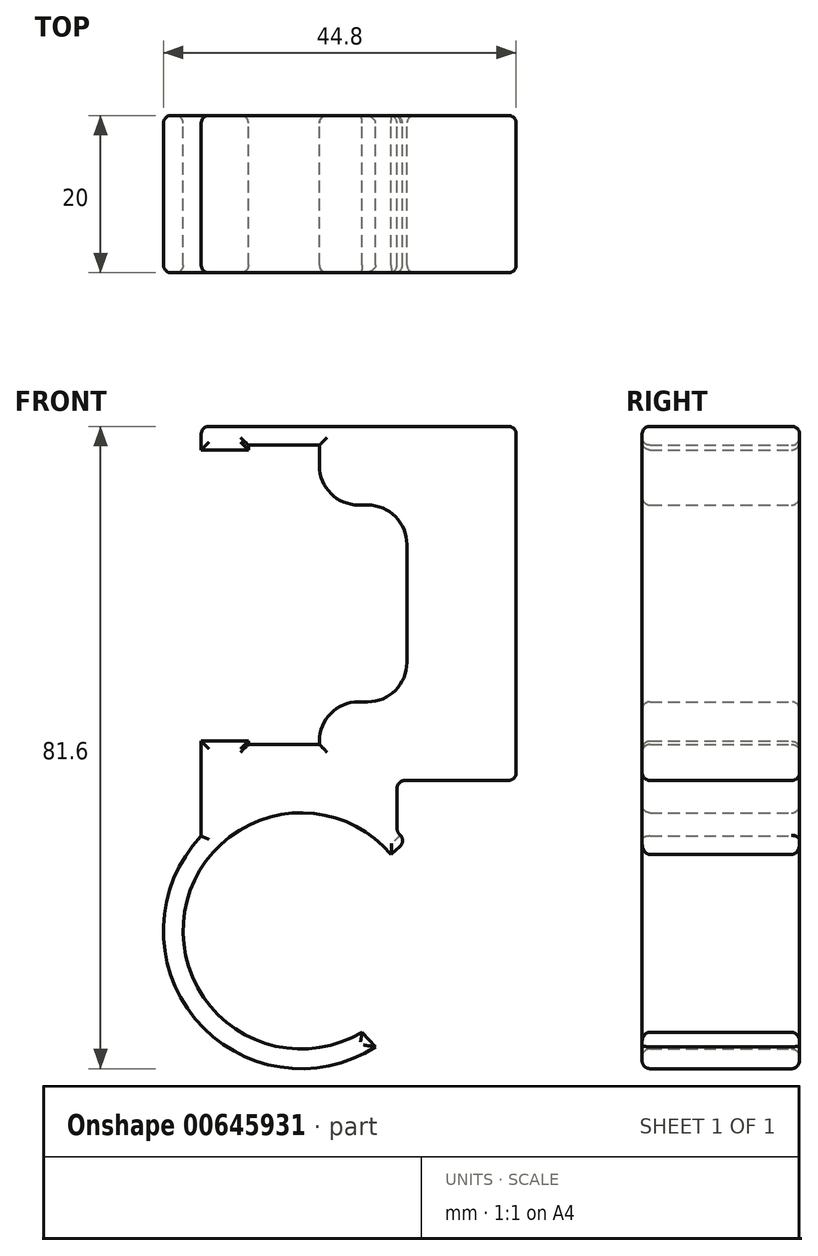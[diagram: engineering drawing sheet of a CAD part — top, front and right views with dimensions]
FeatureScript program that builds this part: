
annotation { "Feature Type Name" : "Feature", "Feature Type Description" : "" }
export const myFeature = defineFeature(function(context is Context, id is Id, definition is map)
    precondition{}
    {
        {
            var Q0;
            Q0=qCreatedBy(makeId("Front.planeOp"),FACE);
            var sketch = newSketch(context, id + "F0", { "sketchPlane" : qUnion([Q0])});
            skArc(sketch, "E0", {"start": v(11.43, 9.71) * mm, "mid": v(-14.8, 2.43) * mm, "end": v(7.72, -12.86) * mm});
            skArc(sketch, "E1", {"start": v(13.28, 11.4) * mm, "mid": v(12.74, 12) * mm, "end": v(12.17, 12.57) * mm});
            skLineSegment(sketch, "E2", {"start": v(11.43, 9.71) * mm, "end": v(13.28, 11.4) * mm});
            skLineSegment(sketch, "E3", {"start": v(7.72, -12.86) * mm, "end": v(9.47, -14.72) * mm});
            skLineSegment(sketch, "E4", {"start": v(-12.7, 17.5) * mm, "end": v(-12.7, 19.1) * mm});
            skLineSegment(sketch, "E5", {"start": v(-12.7, 19.1) * mm, "end": v(12.17, 19.1) * mm});
            skLineSegment(sketch, "E6", {"start": v(12.17, 19.1) * mm, "end": v(12.17, 17.5) * mm});
            skPoint(sketch, "E7.start.orphan", {"position": v(0, 17.5) * mm});
            skLineSegment(sketch, "E8", {"start": v(-12.7, 17.5) * mm, "end": v(-12.7, 12.04) * mm});
            skLineSegment(sketch, "E9", {"start": v(12.17, 17.5) * mm, "end": v(12.17, 12.57) * mm});
            skArc(sketch, "E10.trimOffspring", {"start": v(-12.7, 12.04) * mm, "mid": v(-13.48, -11.16) * mm, "end": v(9.47, -14.72) * mm});
            skSolve(sketch);
        }
        {
            var Q0;
            Q0=makeQuery(id+"F0.imprint","IMPRINT",FACE,{"disambiguationData":[TD([[makeQuery(id+"F0.imprint","IMPRINT",EDGE,{"derivedFrom":sQuery(id+"F0.wireOp",EDGE,"E0")}),-1.0]])]});
            var Q1;
            Q1=makeQuery(id+"F0.imprint","IMPRINT",FACE,{"disambiguationData":[TD([[makeQuery(id+"F0.imprint","IMPRINT",EDGE,{"derivedFrom":sQuery(id+"F0.wireOp",EDGE,"E7")}),-1.0]])]});
            extrude(context, id + "F1", {"entities" : qUnion([Q0, Q1]), "depth" : 20 * mm, "offsetDistance" : 25 * mm});
        }
        {
            var Q0;
            Q0=makeQuery(id+"F1.opExtrude","CAP_FACE",FACE,{"disambiguationData":[OSD([sQuery(id+"F0.wireOp",EDGE,"E0"),sQuery(id+"F0.wireOp",EDGE,"E1"),sQuery(id+"F0.wireOp",EDGE,"E2"),sQuery(id+"F0.wireOp",EDGE,"E3"),sQuery(id+"F0.wireOp",EDGE,"E4"),sQuery(id+"F0.wireOp",EDGE,"E5"),sQuery(id+"F0.wireOp",EDGE,"E6"),sQuery(id+"F0.wireOp",EDGE,"E8"),sQuery(id+"F0.wireOp",EDGE,"E9"),sQuery(id+"F0.wireOp",EDGE,"E10.trimOffspring")])],"isStart":true});
            var sketch = newSketch(context, id + "F2", { "sketchPlane" : qUnion([Q0])});
            skLineSegment(sketch, "E11.bottom", {"start": v(12.7, 19.1) * mm, "end": v(-27.3, 19.1) * mm});
            skLineSegment(sketch, "E11.top", {"start": v(12.7, 64.1) * mm, "end": v(-27.3, 64.1) * mm});
            skLineSegment(sketch, "E11.left", {"start": v(12.7, 19.1) * mm, "end": v(12.7, 64.1) * mm});
            skLineSegment(sketch, "E11.right", {"start": v(-27.3, 19.1) * mm, "end": v(-27.3, 64.1) * mm});
            skLineSegment(sketch, "E12", {"start": v(12.7, 61.1) * mm, "end": v(6.7, 61.1) * mm});
            skLineSegment(sketch, "E13", {"start": v(6.7, 61.7) * mm, "end": v(6.7, 61.1) * mm});
            skLineSegment(sketch, "E14", {"start": v(6.7, 61.7) * mm, "end": v(-2.3, 61.7) * mm});
            skLineSegment(sketch, "E15", {"start": v(12.7, 24.1) * mm, "end": v(6.7, 24.1) * mm});
            skLineSegment(sketch, "E16", {"start": v(6.7, 24.1) * mm, "end": v(6.7, 23.7) * mm});
            skLineSegment(sketch, "E17", {"start": v(6.7, 23.7) * mm, "end": v(-2.3, 23.7) * mm});
            skLineSegment(sketch, "E18", {"start": v(-2.3, 61.7) * mm, "end": v(-2.3, 23.7) * mm});
            skLineSegment(sketch, "E19.bottom", {"start": v(-2.3, 54.1) * mm, "end": v(-13.43, 54.1) * mm});
            skLineSegment(sketch, "E19.top", {"start": v(-2.3, 29.1) * mm, "end": v(-13.43, 29.1) * mm});
            skLineSegment(sketch, "E19.left", {"start": v(-2.3, 54.1) * mm, "end": v(-2.3, 29.1) * mm});
            skLineSegment(sketch, "E19.right", {"start": v(-13.43, 54.1) * mm, "end": v(-13.43, 29.1) * mm});
            skSolve(sketch);
        }
        {
            var Q0;
            {var subQ5=sQuery(id+"F2.wireOp",EDGE,"E11.top");Q0=makeQuery(id+"F2.imprint","IMPRINT",FACE,{"disambiguationData":[TD([[makeQuery(id+"F2.imprint","IMPRINT",EDGE,{"derivedFrom":subQ5}),1.0]])]});}
            extrude(context, id + "F3", {"entities" : qUnion([Q0]), "operationType" : NewBodyOperationType.ADD, "flatOperationType" : FlatOperationType.REMOVE, "oppositeDirection" : true, "depth" : 20 * mm, "offsetDistance" : 25 * mm, "domain" : OperationDomain.MODEL});
        }
        {
            var Q0;
            Q0=makeQuery(id+"F3.opExtrude","SWEPT_EDGE",EDGE,{"disambiguationData":[OSD([sQuery(id+"F2.wireOp",EDGE,"E18"),sQuery(id+"F2.wireOp",EDGE,"E19.bottom"),sQuery(id+"F2.wireOp",EDGE,"E19.left")])]});
            var Q1;
            Q1=makeQuery(id+"F3.opExtrude","SWEPT_EDGE",EDGE,{"disambiguationData":[OSD([sQuery(id+"F2.wireOp",EDGE,"E18"),sQuery(id+"F2.wireOp",EDGE,"E19.top"),sQuery(id+"F2.wireOp",EDGE,"E19.left")])]});
            var Q2;
            Q2=makeQuery(id+"F3.opExtrude","SWEPT_EDGE",EDGE,{"disambiguationData":[OSD([sQuery(id+"F2.wireOp",EDGE,"E19.bottom"),sQuery(id+"F2.wireOp",EDGE,"E19.right")])]});
            var Q3;
            Q3=makeQuery(id+"F3.opExtrude","SWEPT_EDGE",EDGE,{"disambiguationData":[OSD([sQuery(id+"F2.wireOp",EDGE,"E19.top"),sQuery(id+"F2.wireOp",EDGE,"E19.right")])]});
            fillet(context, id + "F4", {"entities" : qUnion([Q0, Q1, Q2, Q3]), "radius" : 5 * mm, "tangentPropagation" : true, "allowEdgeOverflow" : false});
        }
        {
            var Q0;
            Q0=makeQuery(id+"F3.boolean.opBoolean","MERGE",FACE,{"derivedFrom":[makeQuery(id+"F1.opExtrude","CAP_FACE",FACE,{"disambiguationData":[OSD([sQuery(id+"F0.wireOp",EDGE,"E0"),sQuery(id+"F0.wireOp",EDGE,"E1"),sQuery(id+"F0.wireOp",EDGE,"E2"),sQuery(id+"F0.wireOp",EDGE,"E3"),sQuery(id+"F0.wireOp",EDGE,"E4"),sQuery(id+"F0.wireOp",EDGE,"E5"),sQuery(id+"F0.wireOp",EDGE,"E6"),sQuery(id+"F0.wireOp",EDGE,"E8"),sQuery(id+"F0.wireOp",EDGE,"E9"),sQuery(id+"F0.wireOp",EDGE,"E10.trimOffspring")])],"isStart":true}),makeQuery(id+"F3.opExtrude","CAP_FACE",FACE,{"disambiguationData":[OSD([sQuery(id+"F2.wireOp",EDGE,"E11.bottom"),sQuery(id+"F2.wireOp",EDGE,"E11.top"),sQuery(id+"F2.wireOp",EDGE,"E11.left"),sQuery(id+"F2.wireOp",EDGE,"E11.right"),sQuery(id+"F2.wireOp",EDGE,"E12"),sQuery(id+"F2.wireOp",EDGE,"E13"),sQuery(id+"F2.wireOp",EDGE,"E14"),sQuery(id+"F2.wireOp",EDGE,"E15"),sQuery(id+"F2.wireOp",EDGE,"E16"),sQuery(id+"F2.wireOp",EDGE,"E17"),sQuery(id+"F2.wireOp",EDGE,"E18"),sQuery(id+"F2.wireOp",EDGE,"E19.bottom"),sQuery(id+"F2.wireOp",EDGE,"E19.top"),sQuery(id+"F2.wireOp",EDGE,"E19.right")])],"isStart":true})]});
            var Q1;
            Q1=makeQuery(id+"F3.boolean.opBoolean","MERGE",FACE,{"derivedFrom":[makeQuery(id+"F1.opExtrude","CAP_FACE",FACE,{"disambiguationData":[OSD([sQuery(id+"F0.wireOp",EDGE,"E0"),sQuery(id+"F0.wireOp",EDGE,"E1"),sQuery(id+"F0.wireOp",EDGE,"E2"),sQuery(id+"F0.wireOp",EDGE,"E3"),sQuery(id+"F0.wireOp",EDGE,"E4"),sQuery(id+"F0.wireOp",EDGE,"E5"),sQuery(id+"F0.wireOp",EDGE,"E6"),sQuery(id+"F0.wireOp",EDGE,"E8"),sQuery(id+"F0.wireOp",EDGE,"E9"),sQuery(id+"F0.wireOp",EDGE,"E10.trimOffspring")])],"isStart":false}),makeQuery(id+"F3.opExtrude","CAP_FACE",FACE,{"disambiguationData":[OSD([sQuery(id+"F2.wireOp",EDGE,"E11.bottom"),sQuery(id+"F2.wireOp",EDGE,"E11.top"),sQuery(id+"F2.wireOp",EDGE,"E11.left"),sQuery(id+"F2.wireOp",EDGE,"E11.right"),sQuery(id+"F2.wireOp",EDGE,"E12"),sQuery(id+"F2.wireOp",EDGE,"E13"),sQuery(id+"F2.wireOp",EDGE,"E14"),sQuery(id+"F2.wireOp",EDGE,"E15"),sQuery(id+"F2.wireOp",EDGE,"E16"),sQuery(id+"F2.wireOp",EDGE,"E17"),sQuery(id+"F2.wireOp",EDGE,"E18"),sQuery(id+"F2.wireOp",EDGE,"E19.bottom"),sQuery(id+"F2.wireOp",EDGE,"E19.top"),sQuery(id+"F2.wireOp",EDGE,"E19.right")])],"isStart":false})]});
            var Q2;
            Q2=makeQuery(id+"F3.opExtrude","SWEPT_FACE",FACE,{"disambiguationData":[OSD([sQuery(id+"F2.wireOp",EDGE,"E11.top")])]});
            var Q3;
            Q3=makeQuery(id+"F3.opExtrude","SWEPT_FACE",FACE,{"disambiguationData":[OSD([sQuery(id+"F2.wireOp",EDGE,"E11.right")])]});
            var Q4;
            Q4=makeQuery(id+"F3.opExtrude","SWEPT_FACE",FACE,{"disambiguationData":[OSD([sQuery(id+"F2.wireOp",EDGE,"E11.bottom")])]});
            var Q5;
            Q5=makeQuery(id+"F1.opExtrude","SWEPT_FACE",FACE,{"disambiguationData":[OSD([sQuery(id+"F0.wireOp",EDGE,"E6"),sQuery(id+"F0.wireOp",EDGE,"E9")])]});
            var Q6;
            Q6=makeQuery(id+"F1.opExtrude","SWEPT_EDGE",EDGE,{"disambiguationData":[OSD([sQuery(id+"F0.wireOp",EDGE,"E1"),sQuery(id+"F0.wireOp",EDGE,"E2")])]});
            fillet(context, id + "F5", {"entities" : qUnion([Q0, Q1, Q2, Q3, Q4, Q5, Q6]), "radius" : 1 * mm, "tangentPropagation" : true, "allowEdgeOverflow" : false});
        }
    });
